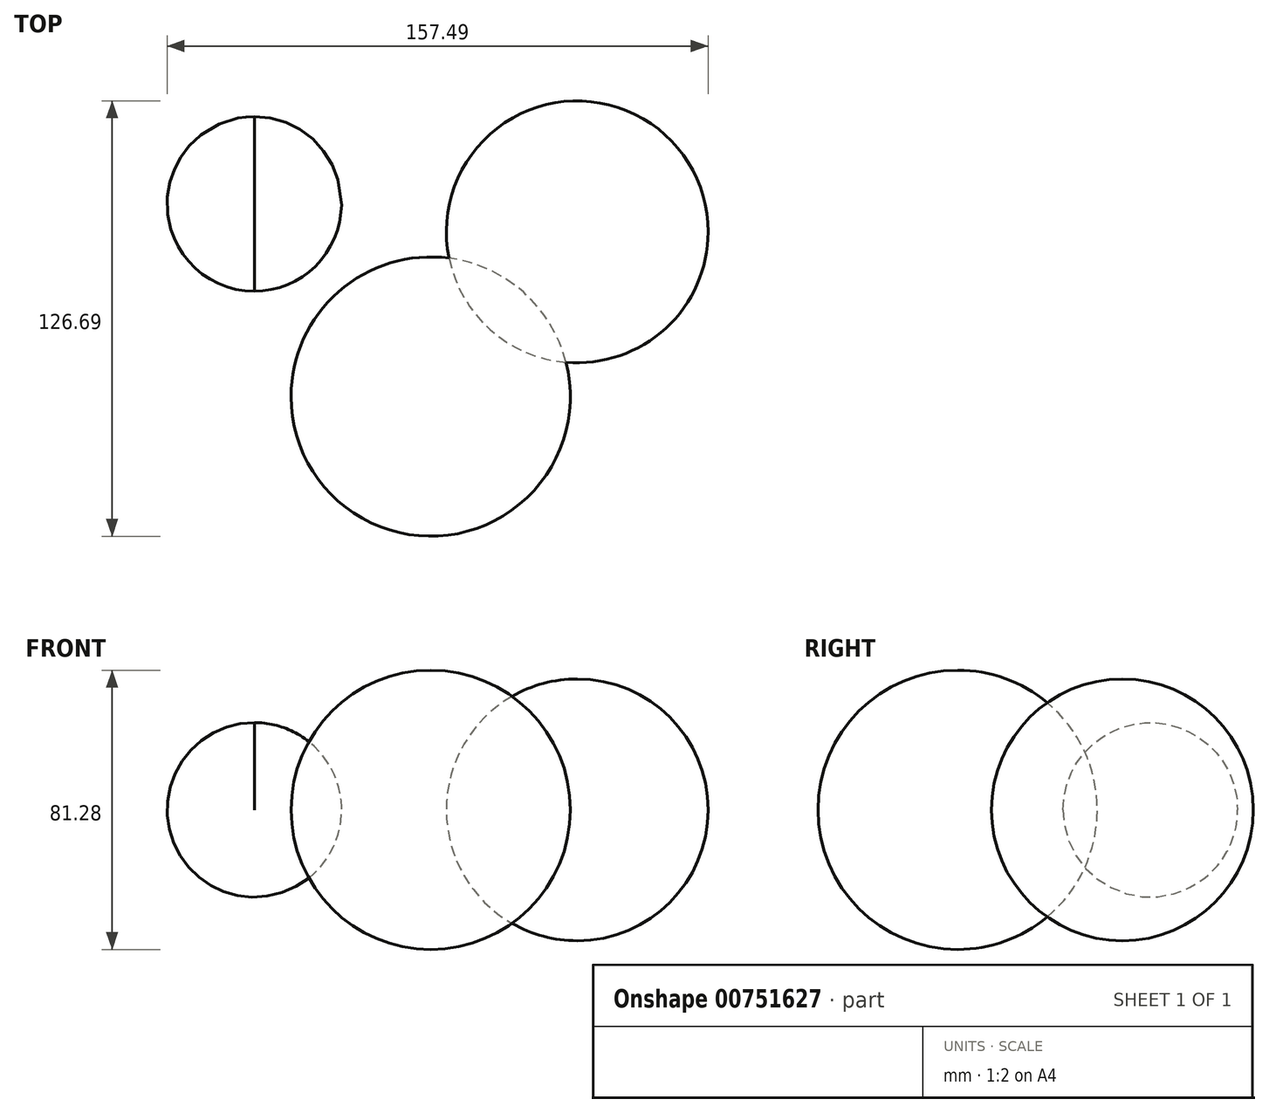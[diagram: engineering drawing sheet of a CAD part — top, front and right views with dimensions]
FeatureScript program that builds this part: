
annotation { "Feature Type Name" : "Feature", "Feature Type Description" : "" }
export const myFeature = defineFeature(function(context is Context, id is Id, definition is map)
    precondition{}
    {
        {
            var Q0;
            Q0=qCreatedBy(makeId("Top.planeOp"),FACE);
            var sketch = newSketch(context, id + "F0", { "sketchPlane" : qUnion([Q0])});
            skCircle(sketch, "E0", {"center": v(42.65, 47.95) * mm, "radius": 38.1 * mm});
            skSolve(sketch);
        }
        {
            var Q0;
            Q0=makeQuery(id+"F0.imprint","IMPRINT",FACE,{"disambiguationData":[TD([[makeQuery(id+"F0.imprint","IMPRINT",EDGE,{"derivedFrom":sQuery(id+"F0.wireOp",EDGE,"E0")}),1.0]])]});
            extrude(context, id + "F1", {"entities" : qUnion([Q0]), "endBound" : BoundingType.SYMMETRIC, "oppositeDirection" : true, "depth" : 76.2 * mm, "offsetDistance" : 25.4 * mm});
        }
        {
            var Q0;
            Q0=qCreatedBy(makeId("Front.planeOp"),FACE);
            var sketch = newSketch(context, id + "F2", { "sketchPlane" : qUnion([Q0])});
            skArc(sketch, "E1", {"start": v(0, -40.64) * mm, "mid": v(40.64, 0) * mm, "end": v(0, 40.64) * mm});
            skLineSegment(sketch, "E2", {"start": v(0, 40.64) * mm, "end": v(0, -40.64) * mm});
            skSolve(sketch);
        }
        {
            var Q0;
            Q0=makeQuery(id+"F2.imprint","IMPRINT",FACE,{"disambiguationData":[TD([[makeQuery(id+"F2.imprint","IMPRINT",EDGE,{"derivedFrom":sQuery(id+"F2.wireOp",EDGE,"E1")}),1.0]])]});
            var Q1;
            Q1=sQuery(id+"F2.wireOp",EDGE,"E1");
            var Q2;
            Q2=sQuery(id+"F2.wireOp",EDGE,"E2");
            revolve(context, id + "F3", {"surfaceOperationType" : NewSurfaceOperationType.NEW, "entities" : qUnion([Q0]), "surfaceEntities" : qUnion([Q1]), "axis" : qUnion([Q2]), "revolveType" : RevolveType.FULL});
        }
        {
            var Q0;
            Q0=makeQuery(id+"F1.opExtrude","CAP_EDGE",EDGE,{"disambiguationData":[OSD([sQuery(id+"F0.wireOp",EDGE,"E0")])],"isStart":false});
            var Q1;
            Q1=makeQuery(id+"F1.opExtrude","CAP_EDGE",EDGE,{"disambiguationData":[OSD([sQuery(id+"F0.wireOp",EDGE,"E0")])],"isStart":true});
            fillet(context, id + "F4", {"entities" : qUnion([Q0, Q1]), "radius" : 38.1 * mm, "tangentPropagation" : true, "allowEdgeOverflow" : false});
        }
        {
            var Q0;
            Q0=qCreatedBy(makeId("Top.planeOp"),FACE);
            var sketch = newSketch(context, id + "F5", { "sketchPlane" : qUnion([Q0])});
            skLineSegment(sketch, "E3", {"start": v(-51.34, 81.5) * mm, "end": v(-51.34, 56.1) * mm});
            skLineSegment(sketch, "E4", {"start": v(-51.34, 56.1) * mm, "end": v(-51.34, 30.7) * mm});
            skSolve(sketch);
        }
        {
            var Q0;
            Q0=sQuery(id+"F5.wireOp",VERTEX,"E3.start");
            var Q1;
            Q1=sQuery(id+"F5.wireOp",EDGE,"E3");
            cPlane(context, id + "F6", {"entities" : qUnion([Q0, Q1]), "cplaneType" : CPlaneType.LINE_POINT, "offset" : 25.4 * mm, "width" : 152.4 * mm, "height" : 152.4 * mm});
        }
        {
            var Q0;
            Q0=sQuery(id+"F5.wireOp",VERTEX,"E4.start");
            var Q1;
            Q1=sQuery(id+"F5.wireOp",EDGE,"E3");
            cPlane(context, id + "F7", {"entities" : qUnion([Q0, Q1]), "cplaneType" : CPlaneType.LINE_POINT, "offset" : 25.4 * mm, "width" : 152.4 * mm, "height" : 152.4 * mm});
        }
        {
            var Q0;
            Q0=sQuery(id+"F5.wireOp",VERTEX,"E4.end");
            var Q1;
            Q1=sQuery(id+"F5.wireOp",EDGE,"E4");
            cPlane(context, id + "F8", {"entities" : qUnion([Q0, Q1]), "cplaneType" : CPlaneType.LINE_POINT, "offset" : 25.4 * mm, "width" : 152.4 * mm, "height" : 152.4 * mm});
        }
        {
            var Q0;
            Q0=qCreatedBy(id+"F6.planeOp",FACE);
            var sketch = newSketch(context, id + "F9", { "sketchPlane" : qUnion([Q0])});
            skPoint(sketch, "E5", {"position": v(-51.34, 0) * mm});
            skSolve(sketch);
        }
        {
            var Q0;
            Q0=qCreatedBy(id+"F8.planeOp",FACE);
            var sketch = newSketch(context, id + "F10", { "sketchPlane" : qUnion([Q0])});
            skPoint(sketch, "E6", {"position": v(-51.34, 0) * mm});
            skSolve(sketch);
        }
        {
            var Q0;
            Q0=qCreatedBy(id+"F7.planeOp",FACE);
            var sketch = newSketch(context, id + "F11", { "sketchPlane" : qUnion([Q0])});
            skCircle(sketch, "E7", {"center": v(-51.34, 0) * mm, "radius": 25.4 * mm});
            skSolve(sketch);
        }
        {
            var Q0;
            Q0=sQuery(id+"F10.wireOp",VERTEX,"E6");
            var Q1;
            Q1=makeQuery(id+"F11.imprint","IMPRINT",FACE,{"disambiguationData":[TD([[makeQuery(id+"F11.imprint","IMPRINT",EDGE,{"derivedFrom":sQuery(id+"F11.wireOp",EDGE,"E7")}),1.0]])]});
            var Q2;
            Q2=sQuery(id+"F9.wireOp",VERTEX,"E5");
            loft(context, id + "F12", {"startCondition" : LoftEndDerivativeType.TANGENT_TO_PROFILE, "startMagnitude" : 1.2, "endCondition" : LoftEndDerivativeType.TANGENT_TO_PROFILE, "endMagnitude" : 1.2, "sheetProfilesArray" : [{ "sheetProfileEntities" : qUnion([Q0]) }, { "sheetProfileEntities" : qUnion([Q1]) }, { "sheetProfileEntities" : qUnion([Q2]) }]});
        }
    });
